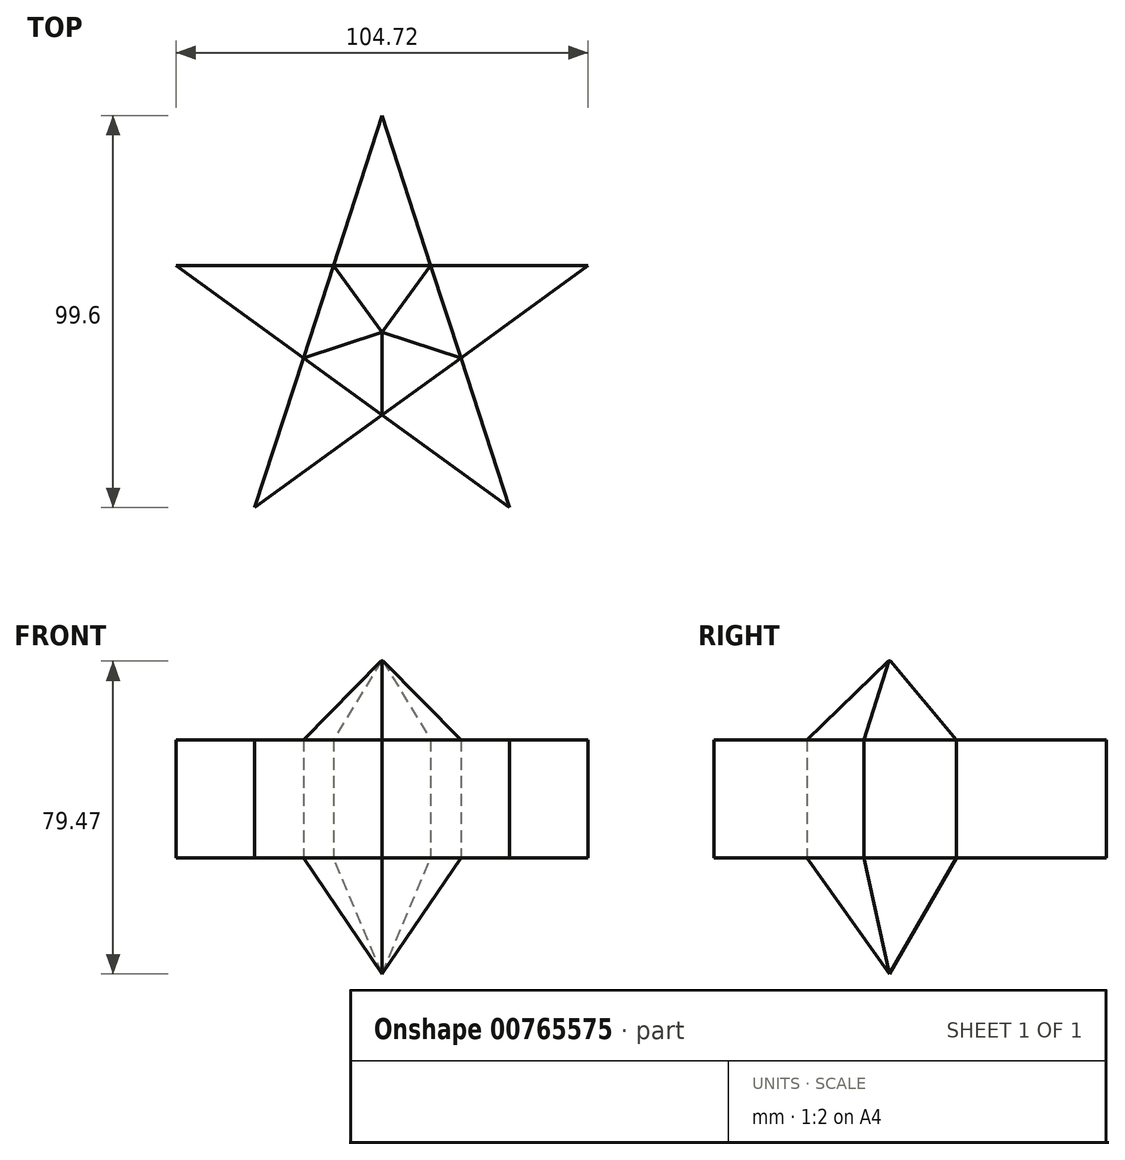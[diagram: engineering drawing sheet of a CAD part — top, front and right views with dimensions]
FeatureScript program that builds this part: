
annotation { "Feature Type Name" : "Feature", "Feature Type Description" : "" }
export const myFeature = defineFeature(function(context is Context, id is Id, definition is map)
    precondition{}
    {
        {
            var Q0;
            Q0=qCreatedBy(makeId("Top.planeOp"),FACE);
            var sketch = newSketch(context, id + "F0", { "sketchPlane" : qUnion([Q0])});
            skCircle(sketch, "E0.cCircle", {"center": v(0, 0) * mm, "radius": 44.54 * mm, "construction": true});
            skLineSegment(sketch, "E0.0", {"start": v(-52.36, 17.01) * mm, "end": v(0, 55.06) * mm, "construction": true});
            skLineSegment(sketch, "E0.1", {"start": v(0, 55.06) * mm, "end": v(52.36, 17.01) * mm, "construction": true});
            skLineSegment(sketch, "E0.2", {"start": v(52.36, 17.01) * mm, "end": v(32.36, -44.54) * mm, "construction": true});
            skLineSegment(sketch, "E0.3", {"start": v(32.36, -44.54) * mm, "end": v(-32.36, -44.54) * mm, "construction": true});
            skLineSegment(sketch, "E0.4", {"start": v(-32.36, -44.54) * mm, "end": v(-52.36, 17.01) * mm, "construction": true});
            skPoint(sketch, "E0.0.midPoint", {"position": v(-26.18, 36.03) * mm});
            skLineSegment(sketch, "E1", {"start": v(-52.36, 17.01) * mm, "end": v(-20, -6.5) * mm});
            skLineSegment(sketch, "E2", {"start": v(-20, -6.5) * mm, "end": v(-32.36, -44.54) * mm});
            skLineSegment(sketch, "E3", {"start": v(-32.36, -44.54) * mm, "end": v(0, -21.03) * mm});
            skLineSegment(sketch, "E4", {"start": v(0, 0) * mm, "end": v(-37.27, 114.7) * mm, "construction": true});
            skLineSegment(sketch, "E5", {"start": v(-37.27, 114.7) * mm, "end": v(0, 0) * mm, "construction": true});
            skLineSegment(sketch, "E6", {"start": v(0, 0) * mm, "end": v(115.65, 37.58) * mm, "construction": true});
            skLineSegment(sketch, "E7", {"start": v(0, 0) * mm, "end": v(37.3, -114.8) * mm, "construction": true});
            skCircle(sketch, "E8.cCircle", {"center": v(0, 0) * mm, "radius": 17.01 * mm, "construction": true});
            skLineSegment(sketch, "E8.0", {"start": v(20, -6.5) * mm, "end": v(0, -21.03) * mm, "construction": true});
            skLineSegment(sketch, "E8.1", {"start": v(0, -21.03) * mm, "end": v(-20, -6.5) * mm, "construction": true});
            skLineSegment(sketch, "E8.2", {"start": v(-20, -6.5) * mm, "end": v(-12.36, 17.01) * mm, "construction": true});
            skLineSegment(sketch, "E8.3", {"start": v(-12.36, 17.01) * mm, "end": v(12.36, 17.01) * mm, "construction": true});
            skLineSegment(sketch, "E8.4", {"start": v(12.36, 17.01) * mm, "end": v(20, -6.5) * mm, "construction": true});
            skPoint(sketch, "E8.0.midPoint", {"position": v(10, -13.76) * mm});
            skLineSegment(sketch, "E9", {"start": v(-52.36, 17.01) * mm, "end": v(-12.36, 17.01) * mm});
            skLineSegment(sketch, "E10", {"start": v(-12.36, 17.01) * mm, "end": v(0, 55.06) * mm});
            skLineSegment(sketch, "E11", {"start": v(0, 55.06) * mm, "end": v(12.36, 17.01) * mm});
            skLineSegment(sketch, "E12", {"start": v(12.36, 17.01) * mm, "end": v(52.36, 17.01) * mm});
            skLineSegment(sketch, "E13", {"start": v(52.36, 17.01) * mm, "end": v(20, -6.5) * mm});
            skLineSegment(sketch, "E14", {"start": v(20, -6.5) * mm, "end": v(32.36, -44.54) * mm});
            skLineSegment(sketch, "E15", {"start": v(32.36, -44.54) * mm, "end": v(0, -21.03) * mm});
            skSolve(sketch);
        }
        {
            var Q0;
            Q0=makeQuery(id+"F0.imprint","IMPRINT",FACE,{"disambiguationData":[TD([[makeQuery(id+"F0.imprint","IMPRINT",EDGE,{"derivedFrom":sQuery(id+"F0.wireOp",EDGE,"E1")}),1.0]])]});
            extrude(context, id + "F1", {"entities" : qUnion([Q0]), "depth" : 30 * mm, "offsetDistance" : 25 * mm});
        }
        {
            var Q0;
            Q0=makeQuery(id+"F1.opExtrude","CAP_FACE",FACE,{"disambiguationData":[OSD([sQuery(id+"F0.wireOp",EDGE,"E1"),sQuery(id+"F0.wireOp",EDGE,"E2"),sQuery(id+"F0.wireOp",EDGE,"E3"),sQuery(id+"F0.wireOp",EDGE,"E9"),sQuery(id+"F0.wireOp",EDGE,"E10"),sQuery(id+"F0.wireOp",EDGE,"E11"),sQuery(id+"F0.wireOp",EDGE,"E12"),sQuery(id+"F0.wireOp",EDGE,"E13"),sQuery(id+"F0.wireOp",EDGE,"E14"),sQuery(id+"F0.wireOp",EDGE,"E15")])],"isStart":false});
            var sketch = newSketch(context, id + "F2", { "sketchPlane" : qUnion([Q0])});
            skLineSegment(sketch, "E16.0", {"start": v(-12.36, 17.01) * mm, "end": v(12.36, 17.01) * mm});
            skLineSegment(sketch, "E17.0", {"start": v(-20, -6.5) * mm, "end": v(-12.36, 17.01) * mm});
            skLineSegment(sketch, "E18.0", {"start": v(0, -21.03) * mm, "end": v(-20, -6.5) * mm});
            skLineSegment(sketch, "E19.0", {"start": v(20, -6.5) * mm, "end": v(0, -21.03) * mm});
            skLineSegment(sketch, "E20.0", {"start": v(12.36, 17.01) * mm, "end": v(20, -6.5) * mm});
            skSolve(sketch);
        }
        {
            var Q0;
            Q0 = qSketchRegion(id + "F2", true);
            extrude(context, id + "F3", {"entities" : qUnion([Q0]), "operationType" : NewBodyOperationType.ADD, "depth" : 20 * mm, "offsetDistance" : 25 * mm, "hasDraft" : true, "draftAngle" : 40 * degree, "draftPullDirection" : true});
        }
        {
            var Q0;
            Q0=qCreatedBy(makeId("Top.planeOp"),FACE);
            var sketch = newSketch(context, id + "F4", { "sketchPlane" : qUnion([Q0])});
            skLineSegment(sketch, "E21.0", {"start": v(0, -21.03) * mm, "end": v(-20, -6.5) * mm});
            skLineSegment(sketch, "E22.0", {"start": v(20, -6.5) * mm, "end": v(0, -21.03) * mm});
            skLineSegment(sketch, "E23.0", {"start": v(12.36, 17.01) * mm, "end": v(20, -6.5) * mm});
            skLineSegment(sketch, "E24.0", {"start": v(-12.36, 17.01) * mm, "end": v(12.36, 17.01) * mm});
            skLineSegment(sketch, "E25.0", {"start": v(-20, -6.5) * mm, "end": v(-12.36, 17.01) * mm});
            skSolve(sketch);
        }
        {
            var Q0;
            Q0 = qSketchRegion(id + "F4", true);
            extrude(context, id + "F5", {"entities" : qUnion([Q0]), "operationType" : NewBodyOperationType.ADD, "oppositeDirection" : true, "depth" : 30 * mm, "offsetDistance" : 25 * mm, "hasDraft" : true, "draftAngle" : 30 * degree, "draftPullDirection" : true});
        }
    });
